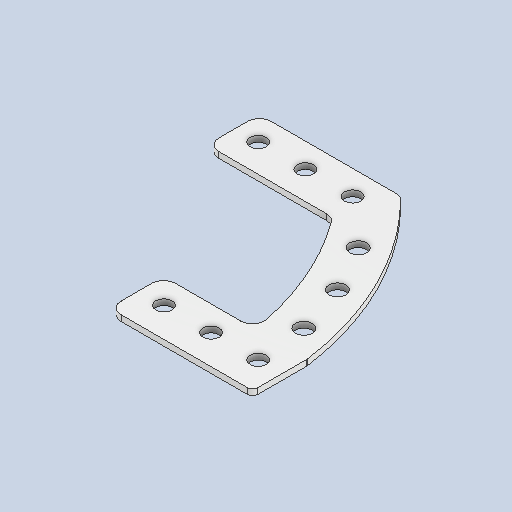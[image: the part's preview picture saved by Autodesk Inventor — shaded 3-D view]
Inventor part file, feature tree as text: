
AUTODESK INVENTOR PART (.ipt)
format: ipt  version: 2025.2 (Build 292293000, 293)  size: 140,288 bytes
history: native  units: in
note: dims shown in document units (in); Inventor stores cm internally (conversion verified against a paired STEP export)
features: other x3, sketch x1
ambient origin geometry x8: Origin, YZ Plane, XZ Plane, XY Plane, X Axis, Y Axis, Z Axis, Center Point
bodies: Solid1 (feature_tree)
feature tree (4):
  other  "Drive_Bumpers.ipt"
  other  "Solid1::Drive_Bumpers.ipt"
  other  "TaggingFeature1"
  sketch  "Sketch1"  dims[d0=0.3937in]
